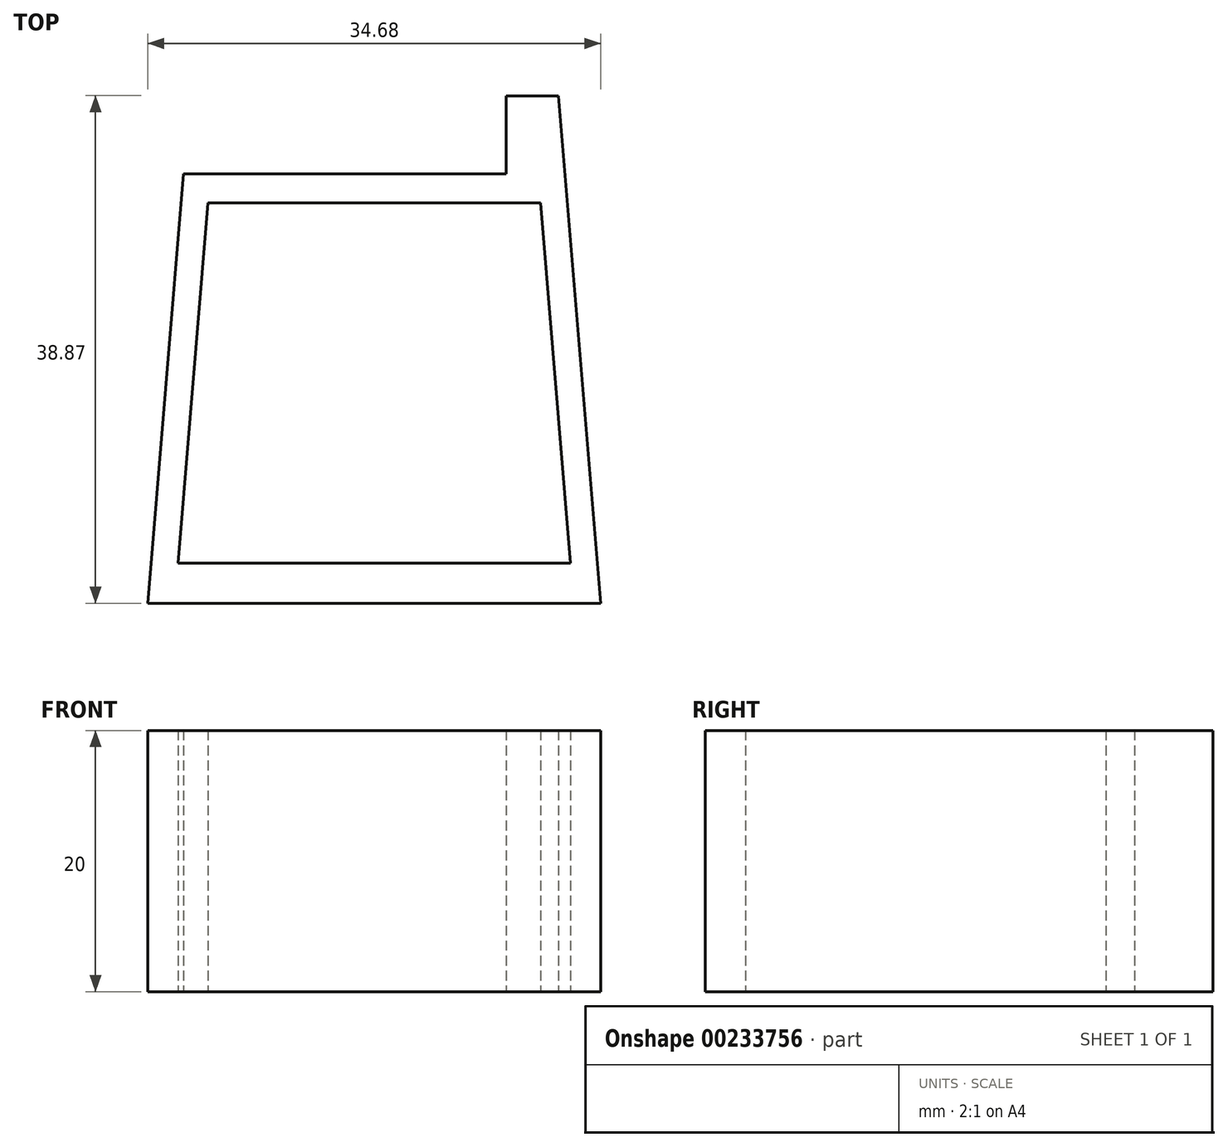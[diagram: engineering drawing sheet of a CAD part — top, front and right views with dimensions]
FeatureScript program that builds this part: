
annotation { "Feature Type Name" : "Feature", "Feature Type Description" : "" }
export const myFeature = defineFeature(function(context is Context, id is Id, definition is map)
    precondition{}
    {
        {
            var Q0;
            Q0=qCreatedBy(makeId("Top.planeOp"),FACE);
            var sketch = newSketch(context, id + "F0", { "sketchPlane" : qUnion([Q0])});
            skLineSegment(sketch, "E0", {"start": v(-10.1, 15.99) * mm, "end": v(0, 15.99) * mm});
            skLineSegment(sketch, "E1.MirrorCS", {"start": v(10.1, 15.99) * mm, "end": v(0, 15.99) * mm});
            skLineSegment(sketch, "E2.MirrorCS", {"start": v(10.1, 21.99) * mm, "end": v(10.1, 15.99) * mm});
            skLineSegment(sketch, "E3.MirrorCS", {"start": v(14.1, 21.99) * mm, "end": v(10.1, 21.99) * mm});
            skLineSegment(sketch, "E4", {"start": v(-17.34, -16.88) * mm, "end": v(0, -16.88) * mm});
            skLineSegment(sketch, "E5.MirrorCS", {"start": v(17.34, -16.88) * mm, "end": v(0, -16.88) * mm});
            skLineSegment(sketch, "E6.MirrorCS", {"start": v(14.1, 21.99) * mm, "end": v(17.34, -16.88) * mm});
            skLineSegment(sketch, "E7", {"start": v(-11.9, -13.81) * mm, "end": v(11.9, -13.81) * mm});
            skPoint(sketch, "E8.trimOffspring.end.orphan", {"position": v(14, -38.92) * mm});
            skPoint(sketch, "E9.MirrorCS.end.orphan", {"position": v(0, -38.92) * mm});
            skPoint(sketch, "E10.trimOffspring.end.orphan", {"position": v(-14, -38.92) * mm});
            skLineSegment(sketch, "E11", {"start": v(-10.1, 15.99) * mm, "end": v(-14.6, 15.99) * mm});
            skLineSegment(sketch, "E12", {"start": v(-14.6, 15.99) * mm, "end": v(-17.34, -16.88) * mm});
            skLineSegment(sketch, "E13", {"start": v(-9.6, 13.78) * mm, "end": v(0, 13.78) * mm});
            skLineSegment(sketch, "E14.MirrorCS", {"start": v(9.6, 13.78) * mm, "end": v(0, 13.78) * mm});
            skLineSegment(sketch, "E15", {"start": v(-11.9, -13.81) * mm, "end": v(-15.03, -13.81) * mm});
            skLineSegment(sketch, "E16", {"start": v(-15.03, -13.81) * mm, "end": v(-12.73, 13.78) * mm});
            skLineSegment(sketch, "E17", {"start": v(-12.73, 13.78) * mm, "end": v(-9.6, 13.78) * mm});
            skLineSegment(sketch, "E18.MirrorCS", {"start": v(15.03, -13.81) * mm, "end": v(12.73, 13.78) * mm});
            skLineSegment(sketch, "E19.MirrorCS", {"start": v(12.73, 13.78) * mm, "end": v(9.6, 13.78) * mm});
            skLineSegment(sketch, "E20.MirrorCS", {"start": v(11.9, -13.81) * mm, "end": v(15.03, -13.81) * mm});
            skPoint(sketch, "E21.MirrorCS.end.orphan", {"position": v(9.6, 13.78) * mm});
            skPoint(sketch, "E21.MirrorCS.start.orphan", {"position": v(9.81, 11.3) * mm});
            skPoint(sketch, "E22.start.orphan", {"position": v(-9.81, 11.3) * mm});
            skSolve(sketch);
        }
        {
            var Q0;
            Q0=makeQuery(id+"F0.imprint","IMPRINT",FACE,{"disambiguationData":[TD([[makeQuery(id+"F0.imprint","IMPRINT",EDGE,{"derivedFrom":sQuery(id+"F0.wireOp",EDGE,"rfD6eyCr-POST-xSWR-9Kmf-QER318G0z96x")}),-1.0]])]});
            var Q1;
            Q1=makeQuery(id+"F0.imprint","IMPRINT",FACE,{"disambiguationData":[TD([[makeQuery(id+"F0.imprint","IMPRINT",EDGE,{"derivedFrom":sQuery(id+"F0.wireOp",EDGE,"E0")}),-1.0]])]});
            extrude(context, id + "F1", {"entities" : qUnion([Q0, Q1]), "depth" : 20 * mm});
        }
    });
